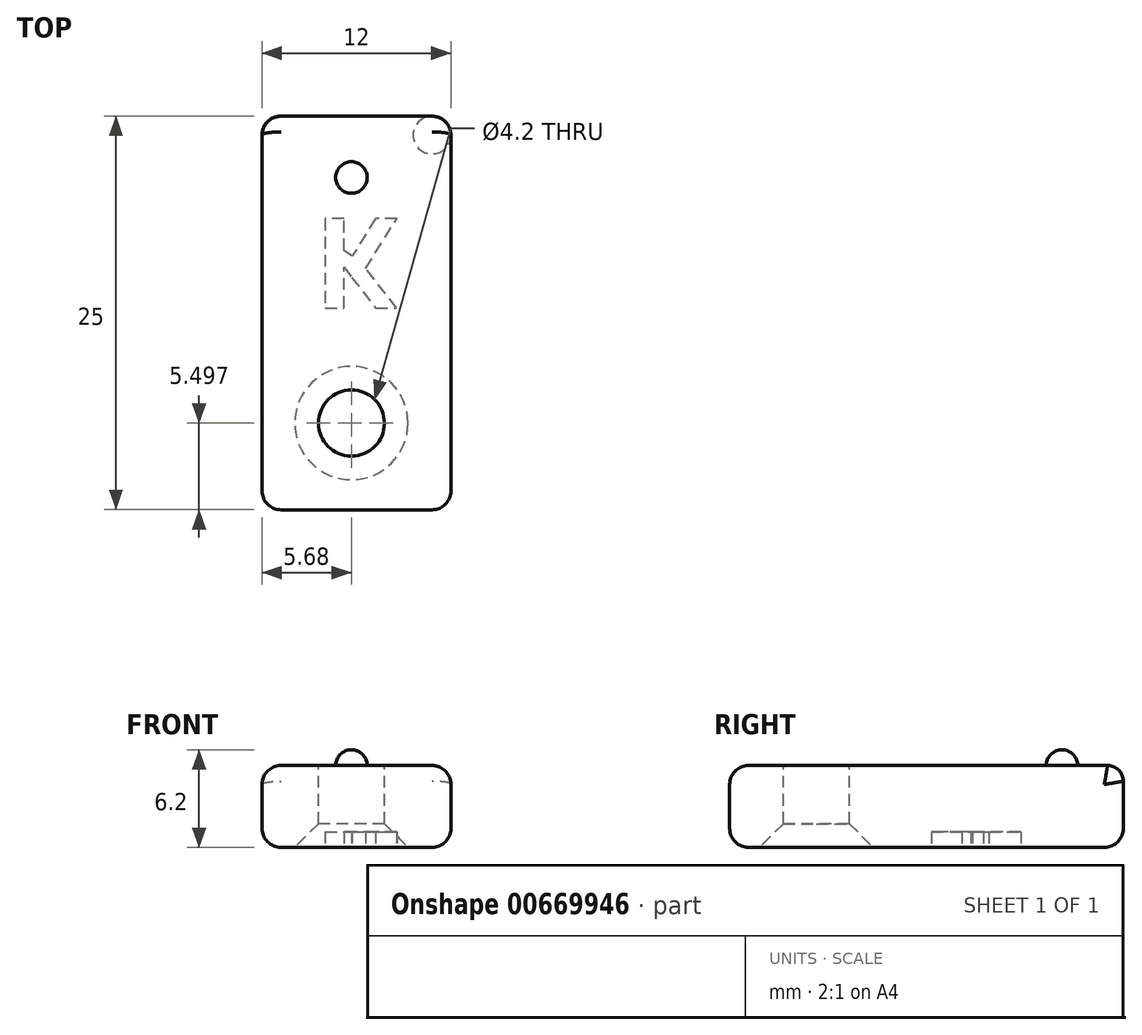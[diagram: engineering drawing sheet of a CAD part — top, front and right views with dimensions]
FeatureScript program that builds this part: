
annotation { "Feature Type Name" : "Feature", "Feature Type Description" : "" }
export const myFeature = defineFeature(function(context is Context, id is Id, definition is map)
    precondition{}
    {
        {
            var Q0;
            Q0=qCreatedBy(makeId("Top.planeOp"),FACE);
            var sketch = newSketch(context, id + "F0", { "sketchPlane" : qUnion([Q0])});
            skLineSegment(sketch, "E0.bottom", {"start": v(-5.68, 13.44) * mm, "end": v(6.32, 13.44) * mm});
            skLineSegment(sketch, "E0.top", {"start": v(-5.68, -11.56) * mm, "end": v(6.32, -11.56) * mm});
            skLineSegment(sketch, "E0.left", {"start": v(-5.68, 13.44) * mm, "end": v(-5.68, -11.56) * mm});
            skLineSegment(sketch, "E0.right", {"start": v(6.32, 13.44) * mm, "end": v(6.32, -11.56) * mm});
            skSolve(sketch);
        }
        {
            var Q0;
            Q0=makeQuery(id+"F0.imprint","IMPRINT",FACE,{"disambiguationData":[TD([[makeQuery(id+"F0.imprint","IMPRINT",EDGE,{"derivedFrom":sQuery(id+"F0.wireOp",EDGE,"E0.bottom")}),-1.0]])]});
            extrude(context, id + "F1", {"entities" : qUnion([Q0]), "depth" : 5.2 * mm, "offsetDistance" : 25 * mm});
        }
        {
            var Q0;
            Q0=makeQuery(id+"F1.opExtrude","CAP_FACE",FACE,{"disambiguationData":[OSD([sQuery(id+"F0.wireOp",EDGE,"E0.bottom"),sQuery(id+"F0.wireOp",EDGE,"E0.top"),sQuery(id+"F0.wireOp",EDGE,"E0.left"),sQuery(id+"F0.wireOp",EDGE,"E0.right")])],"isStart":false});
            var sketch = newSketch(context, id + "F2", { "sketchPlane" : qUnion([Q0])});
            skCircle(sketch, "E1", {"center": v(0, -6.06) * mm, "radius": 2.1 * mm});
            skCircle(sketch, "E2", {"center": v(0, 9.54) * mm, "radius": 1 * mm});
            skSolve(sketch);
        }
        {
            var Q0;
            Q0=makeQuery(id+"F2.imprint","IMPRINT",FACE,{"disambiguationData":[TD([[makeQuery(id+"F2.imprint","IMPRINT",EDGE,{"derivedFrom":sQuery(id+"F2.wireOp",EDGE,"E1")}),1.0]])]});
            var Q1;
            Q1=sQuery(id+"F2.wireOp",EDGE,"E1");
            extrude(context, id + "F3", {"entities" : qUnion([Q0]), "operationType" : NewBodyOperationType.REMOVE, "surfaceEntities" : qUnion([Q1]), "oppositeDirection" : true, "depth" : 25 * mm, "offsetDistance" : 25 * mm});
        }
        {
            var Q0;
            Q0=makeQuery(id+"F2.imprint","IMPRINT",FACE,{"disambiguationData":[TD([[makeQuery(id+"F2.imprint","IMPRINT",EDGE,{"derivedFrom":sQuery(id+"F2.wireOp",EDGE,"E2")}),1.0]])]});
            var Q1;
            Q1=sQuery(id+"F2.wireOp",EDGE,"E2");
            extrude(context, id + "F4", {"entities" : qUnion([Q0]), "operationType" : NewBodyOperationType.ADD, "surfaceEntities" : qUnion([Q1]), "depth" : 1 * mm, "offsetDistance" : 25 * mm});
        }
        {
            var Q0;
            Q0=makeQuery(id+"F4.opExtrude","CAP_EDGE",EDGE,{"disambiguationData":[OSD([sQuery(id+"F2.wireOp",EDGE,"E2")])],"isStart":false});
            fillet(context, id + "F5", {"entities" : qUnion([Q0]), "radius" : 1 * mm, "tangentPropagation" : true, "allowEdgeOverflow" : false});
        }
        {
            var Q0;
            Q0=makeQuery(id+"F1.opExtrude","SWEPT_EDGE",EDGE,{"disambiguationData":[OSD([sQuery(id+"F0.wireOp",EDGE,"E0.bottom"),sQuery(id+"F0.wireOp",EDGE,"E0.right")])]});
            var Q1;
            Q1=makeQuery(id+"F1.opExtrude","SWEPT_EDGE",EDGE,{"disambiguationData":[OSD([sQuery(id+"F0.wireOp",EDGE,"E0.top"),sQuery(id+"F0.wireOp",EDGE,"E0.right")])]});
            var Q2;
            Q2=makeQuery(id+"F1.opExtrude","SWEPT_EDGE",EDGE,{"disambiguationData":[OSD([sQuery(id+"F0.wireOp",EDGE,"E0.top"),sQuery(id+"F0.wireOp",EDGE,"E0.left")])]});
            var Q3;
            Q3=makeQuery(id+"F1.opExtrude","SWEPT_EDGE",EDGE,{"disambiguationData":[OSD([sQuery(id+"F0.wireOp",EDGE,"E0.bottom"),sQuery(id+"F0.wireOp",EDGE,"E0.left")])]});
            var Q4;
            Q4=makeQuery(id+"F1.opExtrude","CAP_EDGE",EDGE,{"disambiguationData":[OSD([sQuery(id+"F0.wireOp",EDGE,"E0.left")])],"isStart":false});
            var Q5;
            Q5=makeQuery(id+"F1.opExtrude","CAP_EDGE",EDGE,{"disambiguationData":[OSD([sQuery(id+"F0.wireOp",EDGE,"E0.right")])],"isStart":false});
            var Q6;
            Q6=makeQuery(id+"F1.opExtrude","CAP_EDGE",EDGE,{"disambiguationData":[OSD([sQuery(id+"F0.wireOp",EDGE,"E0.top")])],"isStart":false});
            var Q7;
            Q7=makeQuery(id+"F1.opExtrude","CAP_EDGE",EDGE,{"disambiguationData":[OSD([sQuery(id+"F0.wireOp",EDGE,"E0.bottom")])],"isStart":true});
            var Q8;
            Q8=makeQuery(id+"F1.opExtrude","CAP_EDGE",EDGE,{"disambiguationData":[OSD([sQuery(id+"F0.wireOp",EDGE,"E0.top")])],"isStart":true});
            var Q9;
            Q9=makeQuery(id+"F1.opExtrude","CAP_EDGE",EDGE,{"disambiguationData":[OSD([sQuery(id+"F0.wireOp",EDGE,"E0.left")])],"isStart":true});
            var Q10;
            Q10=makeQuery(id+"F1.opExtrude","CAP_EDGE",EDGE,{"disambiguationData":[OSD([sQuery(id+"F0.wireOp",EDGE,"E0.right")])],"isStart":true});
            fillet(context, id + "F6", {"entities" : qUnion([Q0, Q1, Q2, Q3, Q4, Q5, Q6, Q7, Q8, Q9, Q10]), "radius" : 1.2 * mm, "tangentPropagation" : true, "allowEdgeOverflow" : false});
        }
        {
            var Q0;
            Q0=makeQuery(id+"F3.boolean.opBoolean","INTERSECT",EDGE,{"derivedFrom":[makeQuery(id+"F1.opExtrude","CAP_FACE",FACE,{"disambiguationData":[OSD([sQuery(id+"F0.wireOp",EDGE,"E0.bottom"),sQuery(id+"F0.wireOp",EDGE,"E0.top"),sQuery(id+"F0.wireOp",EDGE,"E0.left"),sQuery(id+"F0.wireOp",EDGE,"E0.right")])],"isStart":true}),makeQuery(id+"F3.opExtrude","SWEPT_FACE",FACE,{"disambiguationData":[OSD([sQuery(id+"F2.wireOp",EDGE,"E1")])]})]});
            chamfer(context, id + "F7", {"entities" : qUnion([Q0]), "width" : 1.5 * mm, "tangentPropagation" : true});
        }
        {
            var Q0;
            Q0=makeQuery(id+"F1.opExtrude","CAP_FACE",FACE,{"disambiguationData":[OSD([sQuery(id+"F0.wireOp",EDGE,"E0.bottom"),sQuery(id+"F0.wireOp",EDGE,"E0.top"),sQuery(id+"F0.wireOp",EDGE,"E0.left"),sQuery(id+"F0.wireOp",EDGE,"E0.right")])],"isStart":true});
            var sketch = newSketch(context, id + "F8", { "sketchPlane" : qUnion([Q0])});
            skText(sketch, "E3", { "text": "K", "fontName": "OpenSans-Bold.ttf"});
            const initialGuessF8  = {"E3": [-0.00238, -0.00693, 1, 0, 0.00572]};
            skSetInitialGuess(sketch, initialGuessF8);
            skSolve(sketch);
        }
        {
            var Q0;
            Q0 = qSketchRegion(id + "F8", true);
            extrude(context, id + "F9", {"entities" : qUnion([Q0]), "operationType" : NewBodyOperationType.REMOVE, "oppositeDirection" : true, "depth" : 1 * mm, "offsetDistance" : 25 * mm});
        }
        {
            var Q0;
            Q0=makeQuery(id+"F1.opExtrude","CAP_EDGE",EDGE,{"disambiguationData":[OSD([sQuery(id+"F0.wireOp",EDGE,"E0.bottom")])],"isStart":false});
            fillet(context, id + "F10", {"entities" : qUnion([Q0]), "radius" : 1 * mm, "tangentPropagation" : true, "allowEdgeOverflow" : false});
        }
    });
